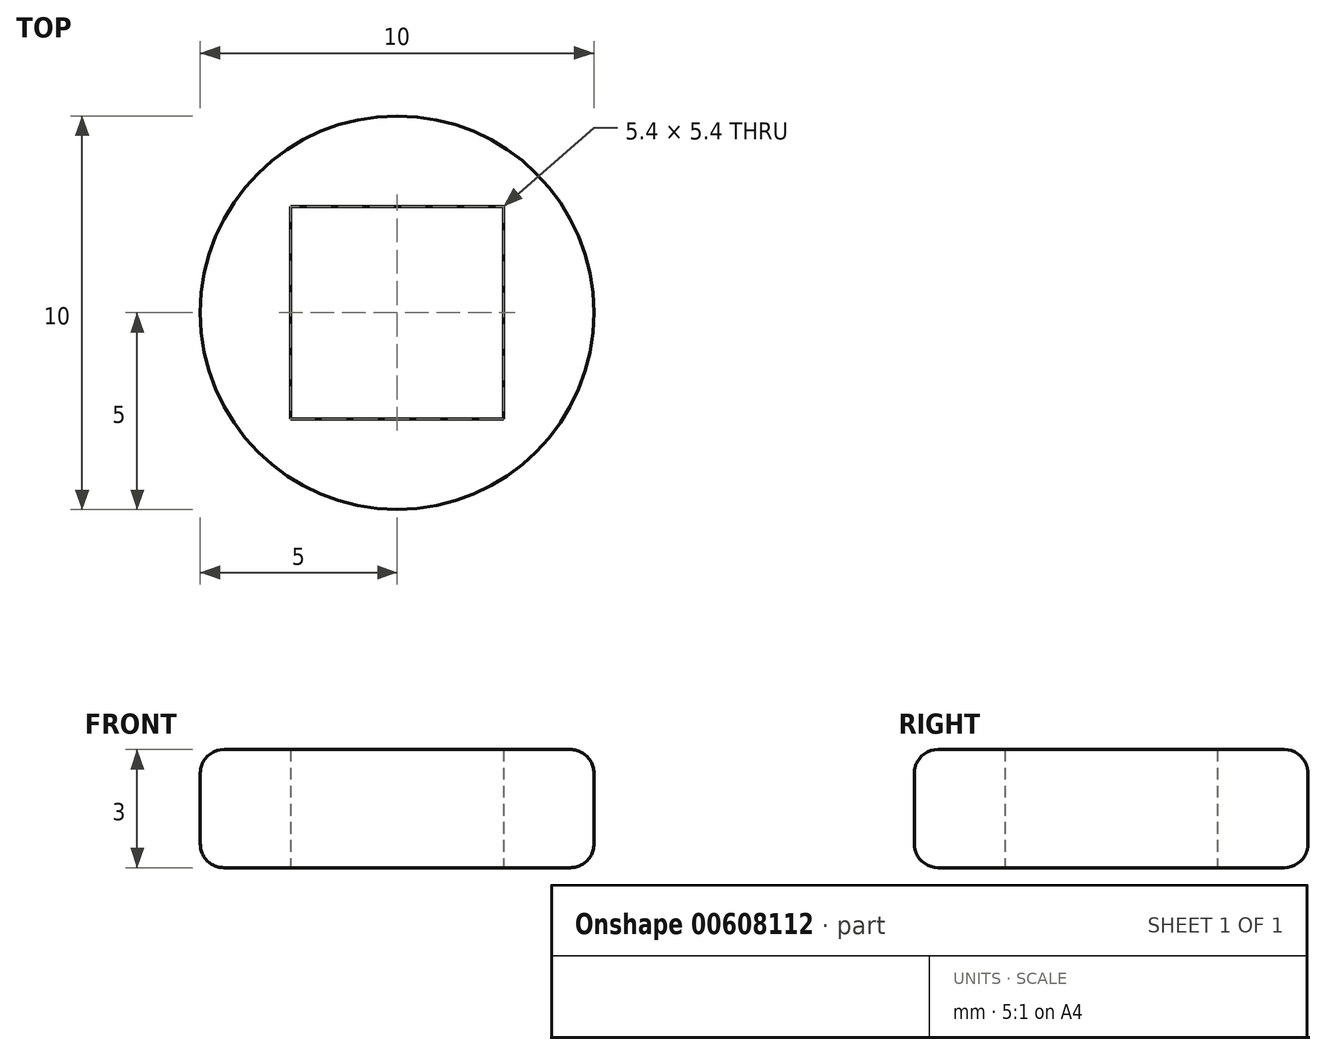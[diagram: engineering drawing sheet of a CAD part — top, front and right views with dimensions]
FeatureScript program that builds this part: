
annotation { "Feature Type Name" : "Feature", "Feature Type Description" : "" }
export const myFeature = defineFeature(function(context is Context, id is Id, definition is map)
    precondition{}
    {
        {
            var Q0;
            Q0=qCreatedBy(makeId("Top.planeOp"),FACE);
            var sketch = newSketch(context, id + "F0", { "sketchPlane" : qUnion([Q0])});
            skCircle(sketch, "E0", {"center": v(0, 0) * mm, "radius": 5 * mm});
            skLineSegment(sketch, "E1.bottom", {"start": v(2.7, -2.7) * mm, "end": v(-2.7, -2.7) * mm});
            skLineSegment(sketch, "E1.top", {"start": v(2.7, 2.7) * mm, "end": v(-2.7, 2.7) * mm});
            skLineSegment(sketch, "E1.left", {"start": v(2.7, -2.7) * mm, "end": v(2.7, 2.7) * mm});
            skLineSegment(sketch, "E1.right", {"start": v(-2.7, -2.7) * mm, "end": v(-2.7, 2.7) * mm});
            skSolve(sketch);
        }
        {
            var Q0;
            Q0=makeQuery(id+"F0.imprint","IMPRINT",FACE,{"disambiguationData":[TD([[makeQuery(id+"F0.imprint","IMPRINT",EDGE,{"derivedFrom":sQuery(id+"F0.wireOp",EDGE,"E0")}),1.0]])]});
            extrude(context, id + "F1", {"entities" : qUnion([Q0]), "depth" : 3 * mm, "offsetDistance" : 25 * mm});
        }
        {
            var Q0;
            Q0=makeQuery(id+"F1.opExtrude","SWEPT_FACE",FACE,{"disambiguationData":[OSD([sQuery(id+"F0.wireOp",EDGE,"E0")])]});
            fillet(context, id + "F2", {"entities" : qUnion([Q0]), "radius" : .6 * mm, "tangentPropagation" : true, "allowEdgeOverflow" : false});
        }
    });
